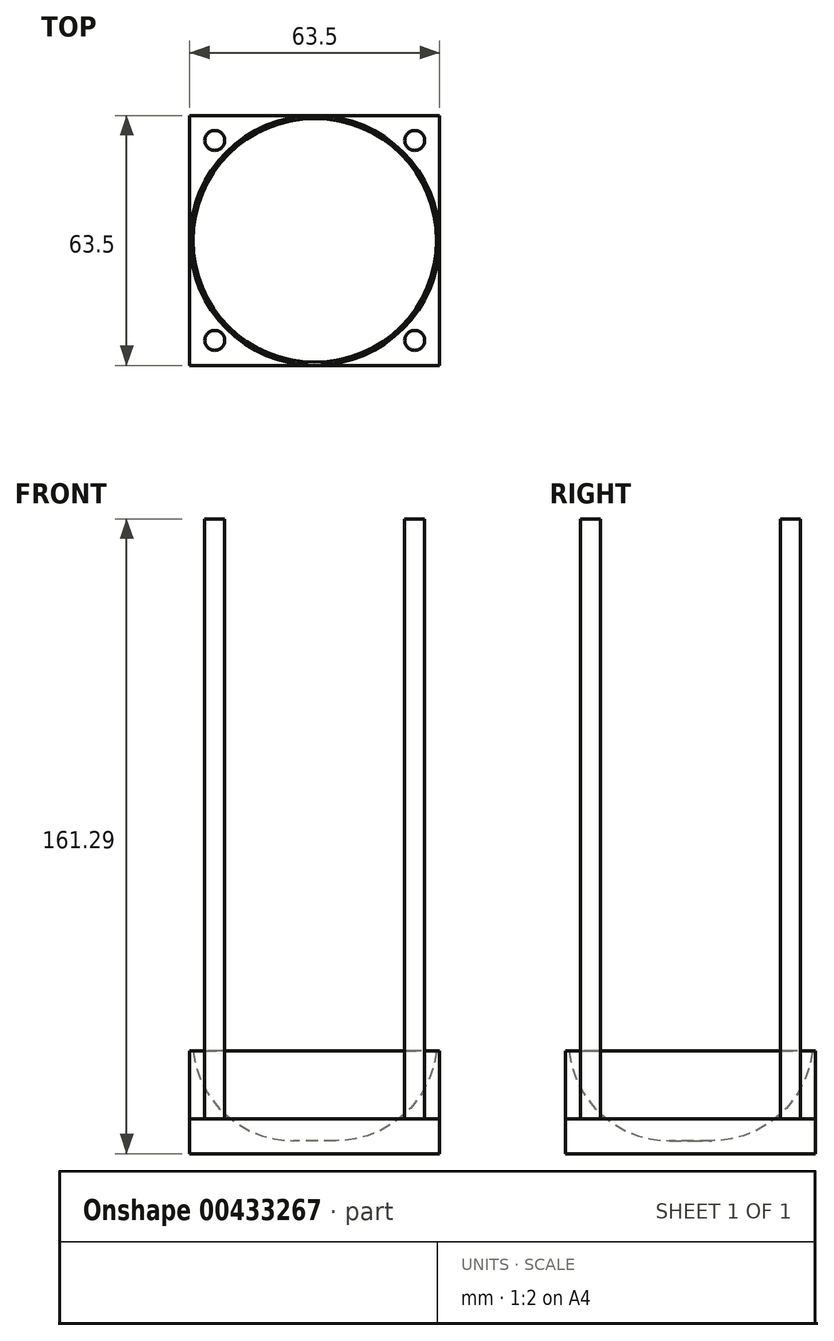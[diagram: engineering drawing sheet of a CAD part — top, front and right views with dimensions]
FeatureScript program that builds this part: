
annotation { "Feature Type Name" : "Feature", "Feature Type Description" : "" }
export const myFeature = defineFeature(function(context is Context, id is Id, definition is map)
    precondition{}
    {
        {
            var Q0;
            Q0=qCreatedBy(makeId("Top.planeOp"),FACE);
            var sketch = newSketch(context, id + "F0", { "sketchPlane" : qUnion([Q0])});
            skLineSegment(sketch, "E0.bottom", {"start": v(31.75, -31.75) * mm, "end": v(-31.75, -31.75) * mm});
            skLineSegment(sketch, "E0.top", {"start": v(31.75, 31.75) * mm, "end": v(-31.75, 31.75) * mm});
            skLineSegment(sketch, "E0.left", {"start": v(31.75, -31.75) * mm, "end": v(31.75, 31.75) * mm});
            skLineSegment(sketch, "E0.right", {"start": v(-31.75, -31.75) * mm, "end": v(-31.75, 31.75) * mm});
            skPoint(sketch, "E0.middle", {"position": v(0, 0) * mm});
            skSolve(sketch);
        }
        {
            var Q0;
            Q0=makeQuery(id+"F0.imprint","IMPRINT",FACE,{"disambiguationData":[TD([[makeQuery(id+"F0.imprint","IMPRINT",EDGE,{"derivedFrom":sQuery(id+"F0.wireOp",EDGE,"E0.bottom")}),-1.0]])]});
            extrude(context, id + "F1", {"entities" : qUnion([Q0]), "depth" : 8.9 * mm});
        }
        {
            var Q0;
            Q0=makeQuery(id+"F1.opExtrude","CAP_FACE",FACE,{"disambiguationData":[OSD([sQuery(id+"F0.wireOp",EDGE,"E0.bottom"),sQuery(id+"F0.wireOp",EDGE,"E0.top"),sQuery(id+"F0.wireOp",EDGE,"E0.left"),sQuery(id+"F0.wireOp",EDGE,"E0.right")])],"isStart":false});
            var sketch = newSketch(context, id + "F2", { "sketchPlane" : qUnion([Q0])});
            skCircle(sketch, "E1", {"center": v(-25.4, 25.4) * mm, "radius": 2.54 * mm});
            skCircle(sketch, "E2.0.1.0", {"center": v(-25.4, -25.4) * mm, "radius": 2.54 * mm});
            skCircle(sketch, "E2.1.0.0", {"center": v(25.4, 25.4) * mm, "radius": 2.54 * mm});
            skCircle(sketch, "E2.1.1.0", {"center": v(25.4, -25.4) * mm, "radius": 2.54 * mm});
            skLineSegment(sketch, "E2.direction1", {"start": v(-25.4, 25.4) * mm, "end": v(25.4, 25.4) * mm, "construction": true});
            skLineSegment(sketch, "E2.direction2", {"start": v(-25.4, 25.4) * mm, "end": v(-25.4, -25.4) * mm, "construction": true});
            skSolve(sketch);
        }
        {
            var Q0;
            Q0=makeQuery(id+"F2.imprint","IMPRINT",FACE,{"disambiguationData":[TD([[makeQuery(id+"F2.imprint","IMPRINT",EDGE,{"derivedFrom":sQuery(id+"F2.wireOp",EDGE,"E2.0.1.0")}),1.0]])]});
            var Q1;
            Q1=makeQuery(id+"F2.imprint","IMPRINT",FACE,{"disambiguationData":[TD([[makeQuery(id+"F2.imprint","IMPRINT",EDGE,{"derivedFrom":sQuery(id+"F2.wireOp",EDGE,"E2.1.1.0")}),1.0]])]});
            var Q2;
            Q2=makeQuery(id+"F2.imprint","IMPRINT",FACE,{"disambiguationData":[TD([[makeQuery(id+"F2.imprint","IMPRINT",EDGE,{"derivedFrom":sQuery(id+"F2.wireOp",EDGE,"E2.1.0.0")}),1.0]])]});
            var Q3;
            Q3=makeQuery(id+"F2.imprint","IMPRINT",FACE,{"disambiguationData":[TD([[makeQuery(id+"F2.imprint","IMPRINT",EDGE,{"derivedFrom":sQuery(id+"F2.wireOp",EDGE,"E1")}),1.0]])]});
            extrude(context, id + "F3", {"entities" : qUnion([Q0, Q1, Q2, Q3]), "operationType" : NewBodyOperationType.ADD, "depth" : 152.4 * mm});
        }
        {
            var Q0;
            Q0=makeQuery(id+"F1.opExtrude","CAP_FACE",FACE,{"disambiguationData":[OSD([sQuery(id+"F0.wireOp",EDGE,"E0.bottom"),sQuery(id+"F0.wireOp",EDGE,"E0.top"),sQuery(id+"F0.wireOp",EDGE,"E0.left"),sQuery(id+"F0.wireOp",EDGE,"E0.right")])],"isStart":false});
            var sketch = newSketch(context, id + "F4", { "sketchPlane" : qUnion([Q0])});
            skCircle(sketch, "E3", {"center": v(0, 0) * mm, "radius": 31.75 * mm});
            skSolve(sketch);
        }
        {
            var Q0;
            {var subQ0=sQuery(id+"F4.wireOp",EDGE,"E3");var subQ1=makeQuery(id+"F4.imprint","INTERSECT",VERTEX,{"derivedFrom":[makeQuery(id+"F1.opExtrude","CAP_EDGE",EDGE,{"disambiguationData":[OSD([sQuery(id+"F0.wireOp",EDGE,"E0.top")])],"isStart":false}),subQ0]});Q0=makeQuery(id+"F4.imprint","IMPRINT",FACE,{"disambiguationData":[TD([[makeQuery(id+"F4.imprint","IMPRINT",EDGE,{"disambiguationData":[TD([[subQ1,1.0]])],"derivedFrom":subQ0}),1.0]])]});}
            extrude(context, id + "F5", {"entities" : qUnion([Q0]), "operationType" : NewBodyOperationType.ADD, "depth" : 2.03 * mm});
        }
        {
            var Q0;
            Q0=makeQuery(id+"F5.opExtrude","CAP_FACE",FACE,{"disambiguationData":[OSD([sQuery(id+"F4.wireOp",EDGE,"E3")])],"isStart":false});
            extrude(context, id + "F6", {"entities" : qUnion([Q0]), "operationType" : NewBodyOperationType.ADD, "depth" : 15.24 * mm});
        }
        {
            var Q0;
            Q0=makeQuery(id+"F6.opExtrude","CAP_FACE",FACE,{"disambiguationData":[OSD([sQuery(id+"F4.wireOp",EDGE,"E3")])],"isStart":false});
            var sketch = newSketch(context, id + "F7", { "sketchPlane" : qUnion([Q0])});
            skCircle(sketch, "E4", {"center": v(0, 0) * mm, "radius": 30.96 * mm});
            skSolve(sketch);
        }
        {
            var Q0;
            Q0=makeQuery(id+"F7.imprint","IMPRINT",FACE,{"disambiguationData":[TD([[makeQuery(id+"F7.imprint","IMPRINT",EDGE,{"derivedFrom":sQuery(id+"F7.wireOp",EDGE,"E4")}),1.0]])]});
            extrude(context, id + "F8", {"entities" : qUnion([Q0]), "operationType" : NewBodyOperationType.REMOVE, "oppositeDirection" : true, "depth" : 2.54 * mm});
        }
        {
            var Q0;
            Q0=makeQuery(id+"F8.boolean.opBoolean","COPY",FACE,{"derivedFrom":makeQuery(id+"F8.opExtrude","CAP_FACE",FACE,{"disambiguationData":[OSD([sQuery(id+"F7.wireOp",EDGE,"E4")])],"isStart":false})});
            extrude(context, id + "F9", {"entities" : qUnion([Q0]), "operationType" : NewBodyOperationType.REMOVE, "oppositeDirection" : true, "depth" : 20.32 * mm});
        }
        {
            var Q0;
            Q0=makeQuery(id+"F9.boolean.opBoolean","COPY",FACE,{"derivedFrom":makeQuery(id+"F9.opExtrude","CAP_FACE",FACE,{"disambiguationData":[OSD([sQuery(id+"F7.wireOp",EDGE,"E4")])],"isStart":false})});
            fillet(context, id + "F10", {"entities" : qUnion([Q0]), "radius" : 25.75 * mm, "tangentPropagation" : true, "allowEdgeOverflow" : false});
        }
    });
